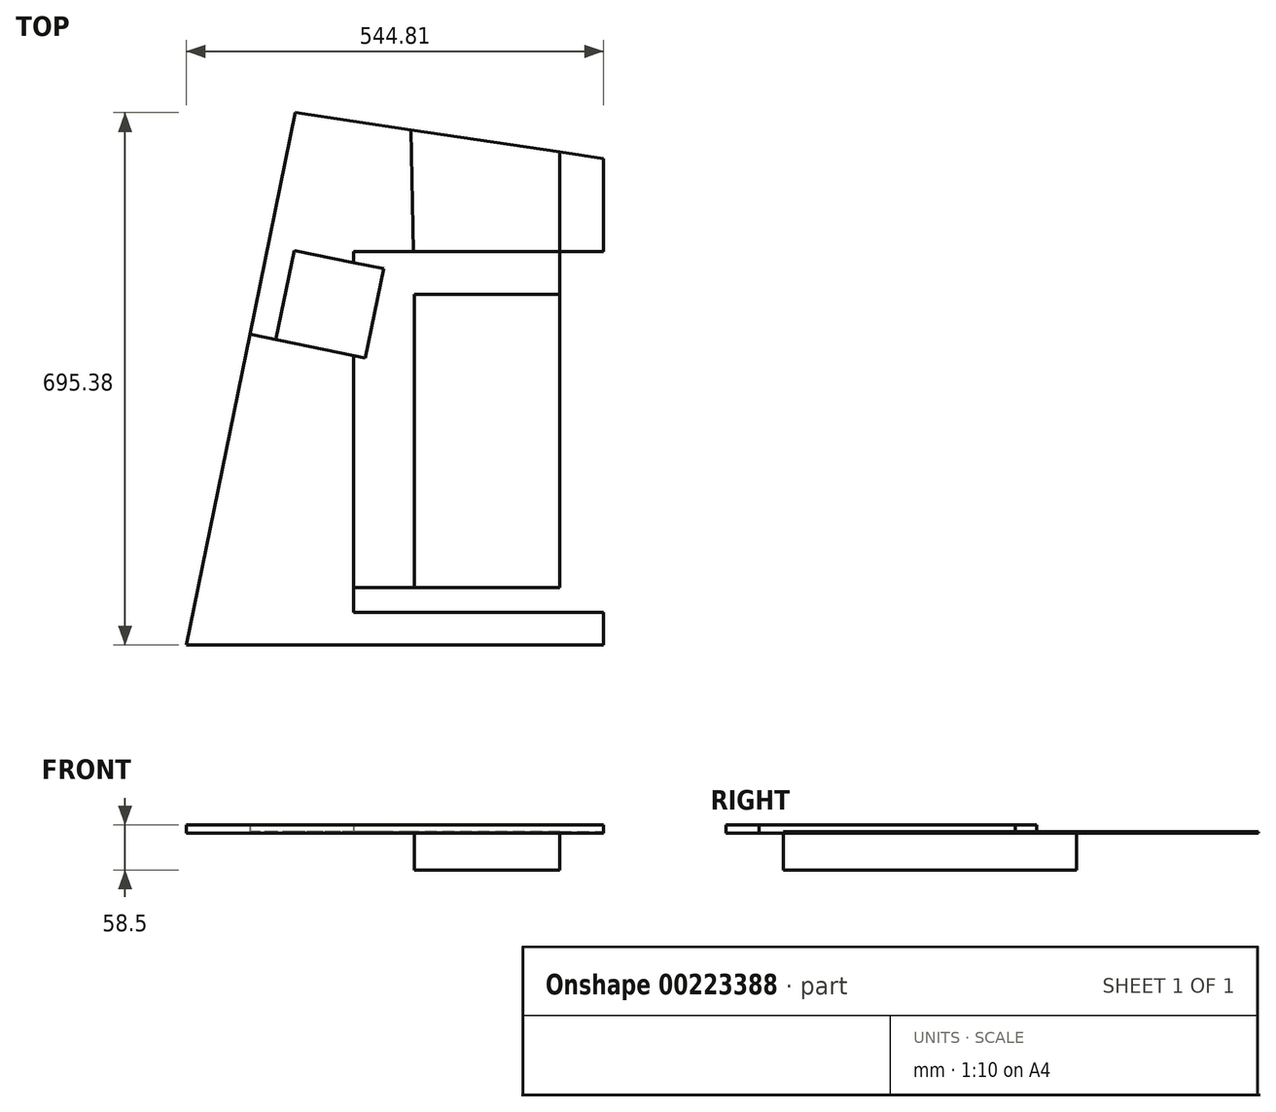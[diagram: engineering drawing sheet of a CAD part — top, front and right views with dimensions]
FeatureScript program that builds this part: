
annotation { "Feature Type Name" : "Feature", "Feature Type Description" : "" }
export const myFeature = defineFeature(function(context is Context, id is Id, definition is map)
    precondition{}
    {
        {
            var Q0;
            Q0=qCreatedBy(makeId("Top.planeOp"),FACE);
            var sketch = newSketch(context, id + "F0", { "sketchPlane" : qUnion([Q0])});
            skLineSegment(sketch, "E0", {"start": v(-196.34, 336.38) * mm, "end": v(-323.41, -284) * mm});
            skLineSegment(sketch, "E1", {"start": v(-323.41, -284) * mm, "end": v(149.04, -284) * mm});
            skLineSegment(sketch, "E2", {"start": v(149.04, -284) * mm, "end": v(149.04, 285) * mm, "construction": true});
            skLineSegment(sketch, "E3", {"start": v(149.04, 285) * mm, "end": v(-196.34, 336.38) * mm});
            skLineSegment(sketch, "E4", {"start": v(-244.96, 99) * mm, "end": v(149.04, 99) * mm, "construction": true});
            skLineSegment(sketch, "E5", {"start": v(-40.96, 99) * mm, "end": v(-45.57, 313.95) * mm, "construction": true});
            skLineSegment(sketch, "E6", {"start": v(149.04, 99) * mm, "end": v(149.04, -284) * mm});
            skLineSegment(sketch, "E7.bottom", {"start": v(-40.96, 99) * mm, "end": v(149.04, 99) * mm});
            skLineSegment(sketch, "E7.top", {"start": v(-40.96, -284) * mm, "end": v(149.04, -284) * mm});
            skLineSegment(sketch, "E7.left", {"start": v(-40.96, 99) * mm, "end": v(-40.96, -284) * mm});
            skLineSegment(sketch, "E8", {"start": v(-323.41, -284) * mm, "end": v(-338.77, -359) * mm});
            skLineSegment(sketch, "E9", {"start": v(-338.77, -359) * mm, "end": v(149.04, -359) * mm});
            skLineSegment(sketch, "E10", {"start": v(149.04, -359) * mm, "end": v(149.04, -284) * mm});
            skPoint(sketch, "E11", {"position": v(-40.96, 16) * mm});
            skLineSegment(sketch, "E12", {"start": v(-40.96, 16) * mm, "end": v(-261.96, 16) * mm, "construction": true});
            skLineSegment(sketch, "E13", {"start": v(149.04, 285) * mm, "end": v(206.04, 276.52) * mm});
            skLineSegment(sketch, "E14", {"start": v(206.04, 276.52) * mm, "end": v(206.04, -359) * mm});
            skLineSegment(sketch, "E15", {"start": v(206.04, -359) * mm, "end": v(149.04, -359) * mm});
            skLineSegment(sketch, "E16", {"start": v(206.04, 155) * mm, "end": v(-233.5, 155) * mm, "construction": true});
            skLineSegment(sketch, "E17", {"start": v(206.04, -316) * mm, "end": v(-119.96, -316) * mm});
            skLineSegment(sketch, "E18", {"start": v(-119.96, -316) * mm, "end": v(-119.96, 155) * mm});
            skLineSegment(sketch, "E19", {"start": v(-119.96, 155) * mm, "end": v(206.04, 155) * mm});
            skLineSegment(sketch, "E20", {"start": v(-197.82, 156.45) * mm, "end": v(-221.7, 39.87) * mm});
            skLineSegment(sketch, "E21", {"start": v(-221.7, 39.87) * mm, "end": v(-105.12, 16) * mm});
            skLineSegment(sketch, "E22", {"start": v(-105.12, 16) * mm, "end": v(-81.24, 132.58) * mm});
            skLineSegment(sketch, "E23", {"start": v(-81.24, 132.58) * mm, "end": v(-197.82, 156.45) * mm});
            skLineSegment(sketch, "E24", {"start": v(-221.7, 39.87) * mm, "end": v(-255.65, 46.83) * mm});
            skLineSegment(sketch, "E25", {"start": v(-40.96, 99) * mm, "end": v(-45.57, 313.95) * mm});
            skLineSegment(sketch, "E26", {"start": v(149.04, 99) * mm, "end": v(149.04, 285) * mm});
            skSolve(sketch);
        }
        {
            var Q0;
            Q0=makeQuery(id+"F0.imprint","IMPRINT",FACE,{"disambiguationData":[TD([[makeQuery(id+"F0.imprint","IMPRINT",EDGE,{"derivedFrom":sQuery(id+"F0.wireOp",EDGE,"E7.bottom")}),-1.0]])]});
            extrude(context, id + "F1", {"entities" : qUnion([Q0]), "oppositeDirection" : true, "offsetDistance" : 25 * mm, "depth" : 48 * mm});
        }
        {
            var Q0;
            Q0=makeQuery(id+"F0.imprint","IMPRINT",FACE,{"disambiguationData":[TD([[makeQuery(id+"F0.imprint","IMPRINT",EDGE,{"derivedFrom":sQuery(id+"F0.wireOp",EDGE,"E7.bottom")}),1.0]])]});
            var Q1;
            {var subQ1=sQuery(id+"F0.wireOp",EDGE,"E7.top");Q1=makeQuery(id+"F0.imprint","IMPRINT",FACE,{"disambiguationData":[TD([[makeQuery(id+"F0.imprint","IMPRINT",EDGE,{"derivedFrom":subQ1}),-1.0]])]});}
            var Q2;
            {var subQ6=sQuery(id+"F0.wireOp",EDGE,"E7.left");Q2=makeQuery(id+"F0.imprint","IMPRINT",FACE,{"disambiguationData":[TD([[makeQuery(id+"F0.imprint","IMPRINT",EDGE,{"derivedFrom":subQ6}),-1.0]])]});}
            var Q3;
            {var subQ8=sQuery(id+"F0.wireOp",EDGE,"E6");Q3=makeQuery(id+"F0.imprint","IMPRINT",FACE,{"disambiguationData":[TD([[makeQuery(id+"F0.imprint","IMPRINT",EDGE,{"derivedFrom":subQ8}),1.0]])]});}
            extrude(context, id + "F2", {"entities" : qUnion([Q0, Q1, Q2, Q3]), "offsetDistance" : 25 * mm, "depth" : 2 * mm});
        }
        {
            var Q0;
            {var subQ0=sQuery(id+"F0.wireOp",EDGE,"E24");Q0=makeQuery(id+"F0.imprint","IMPRINT",FACE,{"disambiguationData":[TD([[makeQuery(id+"F0.imprint","IMPRINT",EDGE,{"derivedFrom":subQ0}),1.0]])]});}
            var Q1;
            {var subQ4=sQuery(id+"F0.wireOp",EDGE,"E8");Q1=makeQuery(id+"F0.imprint","IMPRINT",FACE,{"disambiguationData":[TD([[makeQuery(id+"F0.imprint","IMPRINT",EDGE,{"derivedFrom":subQ4}),1.0]])]});}
            var Q2;
            {var subQ0=sQuery(id+"F0.wireOp",EDGE,"E15");Q2=makeQuery(id+"F0.imprint","IMPRINT",FACE,{"disambiguationData":[TD([[makeQuery(id+"F0.imprint","IMPRINT",EDGE,{"derivedFrom":subQ0}),-1.0]])]});}
            extrude(context, id + "F3", {"entities" : qUnion([Q0, Q1, Q2]), "offsetDistance" : 25 * mm, "depth" : 10.5 * mm});
        }
        {
            var Q0;
            {var subQ5=sQuery(id+"F0.wireOp",EDGE,"E3");Q0=makeQuery(id+"F0.imprint","IMPRINT",FACE,{"disambiguationData":[TD([[makeQuery(id+"F0.imprint","IMPRINT",EDGE,{"derivedFrom":subQ5}),1.0]])]});}
            extrude(context, id + "F4", {"entities" : qUnion([Q0]), "offsetDistance" : 25 * mm, "depth" : 2 * mm});
        }
        {
            var Q0;
            {var subQ12=sQuery(id+"F0.wireOp",EDGE,"E20");Q0=makeQuery(id+"F0.imprint","IMPRINT",FACE,{"disambiguationData":[TD([[makeQuery(id+"F0.imprint","IMPRINT",EDGE,{"derivedFrom":subQ12}),-1.0]])]});}
            var Q1;
            {var subQ0=sQuery(id+"F0.wireOp",EDGE,"E13");Q1=makeQuery(id+"F0.imprint","IMPRINT",FACE,{"disambiguationData":[TD([[makeQuery(id+"F0.imprint","IMPRINT",EDGE,{"derivedFrom":subQ0}),-1.0]])]});}
            var Q2;
            Q2=makeQuery(id+"F4.opExtrude","CAP_FACE",FACE,{"disambiguationData":[OSD([sQuery(id+"F0.wireOp",EDGE,"E3"),sQuery(id+"F0.wireOp",EDGE,"E19"),sQuery(id+"F0.wireOp",EDGE,"E25"),sQuery(id+"F0.wireOp",EDGE,"E26")])],"isStart":false});
            extrude(context, id + "F5", {"entities" : qUnion([Q0, Q1]), "endBound" : BoundingType.UP_TO_SURFACE, "depth" : 25 * mm, "endBoundEntityFace" : qUnion([Q2]), "offsetDistance" : 25 * mm});
        }
    });
